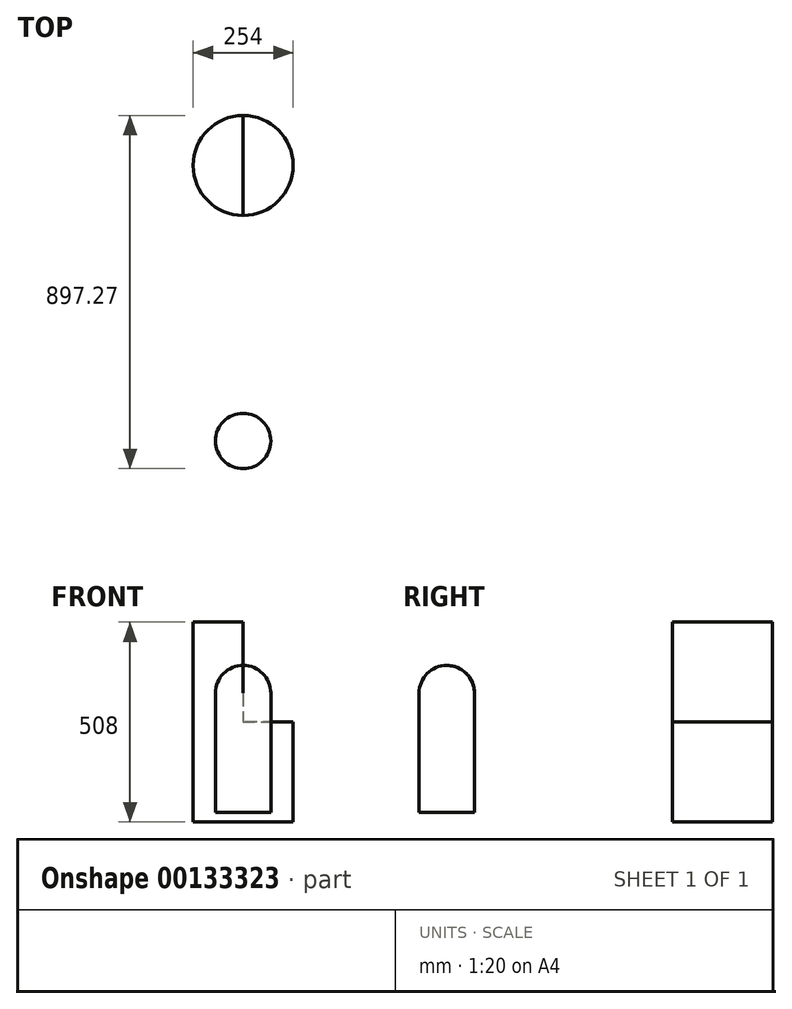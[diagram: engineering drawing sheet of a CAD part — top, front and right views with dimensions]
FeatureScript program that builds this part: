
annotation { "Feature Type Name" : "Feature", "Feature Type Description" : "" }
export const myFeature = defineFeature(function(context is Context, id is Id, definition is map)
    precondition{}
    {
        {
            var Q0;
            Q0=qCreatedBy(makeId("Top.planeOp"),FACE);
            var sketch = newSketch(context, id + "F0", { "sketchPlane" : qUnion([Q0])});
            skCircle(sketch, "E0", {"center": v(0, 0) * mm, "radius": 127 * mm});
            skSolve(sketch);
        }
        {
            var Q0;
            Q0 = qSketchRegion(id + "F0", true);
            extrude(context, id + "F1", {"entities" : qUnion([Q0]), "depth" : 508 * mm});
        }
        {
            var Q0;
            Q0=qCreatedBy(makeId("Right.planeOp"),FACE);
            var sketch = newSketch(context, id + "F2", { "sketchPlane" : qUnion([Q0])});
            skLineSegment(sketch, "E1.bottom", {"start": v(-183.48, 679.65) * mm, "end": v(227.67, 679.65) * mm});
            skLineSegment(sketch, "E1.top", {"start": v(-183.48, 254) * mm, "end": v(227.67, 254) * mm});
            skLineSegment(sketch, "E1.left", {"start": v(-183.48, 679.65) * mm, "end": v(-183.48, 254) * mm});
            skLineSegment(sketch, "E1.right", {"start": v(227.67, 679.65) * mm, "end": v(227.67, 254) * mm});
            skSolve(sketch);
        }
        {
            var Q0;
            Q0 = qSketchRegion(id + "F2", true);
            extrude(context, id + "F3", {"entities" : qUnion([Q0]), "operationType" : NewBodyOperationType.REMOVE, "endBound" : BoundingType.THROUGH_ALL, "depth" : 25.4 * mm});
        }
        {
            var Q0;
            Q0=qCreatedBy(makeId("Right.planeOp"),FACE);
            var sketch = newSketch(context, id + "F4", { "sketchPlane" : qUnion([Q0])});
            skArc(sketch, "E2", {"start": v(-699.98, 397.96) * mm, "mid": v(-749.68, 377.37) * mm, "end": v(-770.27, 327.66) * mm});
            skLineSegment(sketch, "E3.bottom", {"start": v(-699.98, 24.62) * mm, "end": v(-770.27, 24.62) * mm});
            skLineSegment(sketch, "E3.right", {"start": v(-770.27, 24.62) * mm, "end": v(-770.27, 327.66) * mm});
            skLineSegment(sketch, "E4", {"start": v(-699.98, 24.62) * mm, "end": v(-699.98, 327.66) * mm});
            skLineSegment(sketch, "E5", {"start": v(-699.98, 327.66) * mm, "end": v(-699.98, 397.96) * mm});
            skSolve(sketch);
        }
        {
            var Q0;
            Q0 = qSketchRegion(id + "F4", true);
            var Q1;
            Q1=sQuery(id+"F4.wireOp",EDGE,"E4");
            revolve(context, id + "F5", {"entities" : qUnion([Q0]), "axis" : qUnion([Q1]), "revolveType" : RevolveType.FULL});
        }
    });
